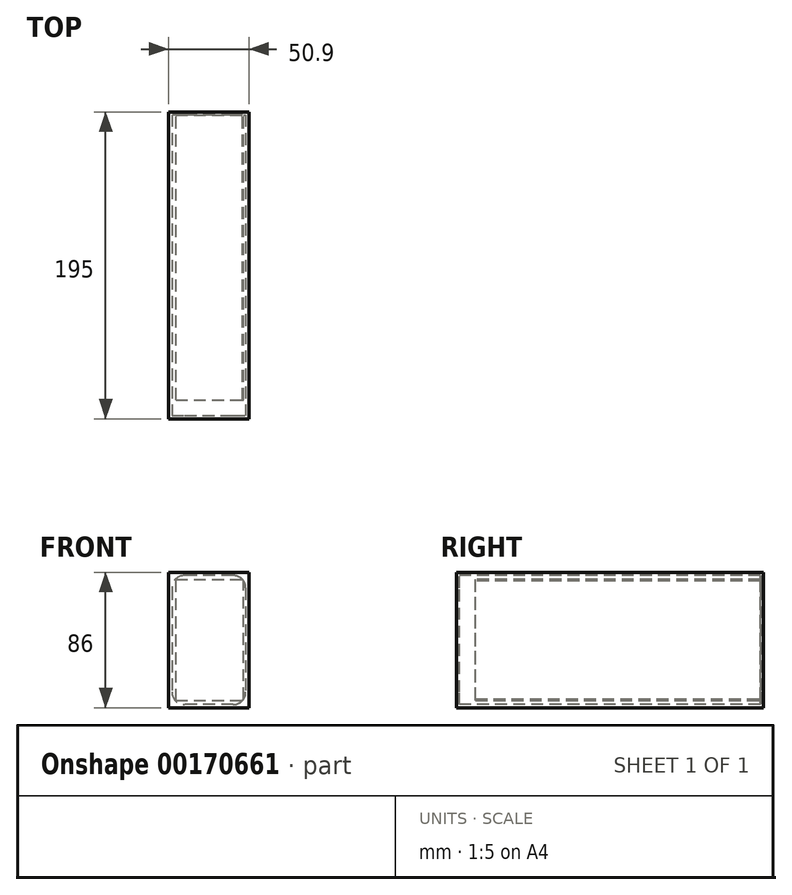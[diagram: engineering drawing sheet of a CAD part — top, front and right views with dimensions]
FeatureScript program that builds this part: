
annotation { "Feature Type Name" : "Feature", "Feature Type Description" : "" }
export const myFeature = defineFeature(function(context is Context, id is Id, definition is map)
    precondition{}
    {
        {
            var Q0;
            Q0=qCreatedBy(makeId("Front.planeOp"),FACE);
            var sketch = newSketch(context, id + "F0", { "sketchPlane" : qUnion([Q0])});
            skLineSegment(sketch, "E0.bottom", {"start": v(-21.5, -38.5) * mm, "end": v(21.5, -38.5) * mm});
            skLineSegment(sketch, "E0.top", {"start": v(-21.5, 38.5) * mm, "end": v(21.5, 38.5) * mm});
            skLineSegment(sketch, "E0.left", {"start": v(-21.5, -38.5) * mm, "end": v(-21.5, 38.5) * mm});
            skLineSegment(sketch, "E0.right", {"start": v(21.5, -38.5) * mm, "end": v(21.5, 38.5) * mm});
            skPoint(sketch, "E0.middle", {"position": v(0, 0) * mm});
            skSolve(sketch);
        }
        {
            var Q0;
            Q0 = qSketchRegion(id + "F0", true);
            extrude(context, id + "F1", {"entities" : qUnion([Q0]), "depth" : 181 * mm});
        }
        {
            var Q0;
            Q0=makeQuery(id+"F1.opExtrude","CAP_FACE",FACE,{"disambiguationData":[OSD([sQuery(id+"F0.wireOp",EDGE,"E0.bottom"),sQuery(id+"F0.wireOp",EDGE,"E0.top"),sQuery(id+"F0.wireOp",EDGE,"E0.left"),sQuery(id+"F0.wireOp",EDGE,"E0.right")])],"isStart":false});
            var sketch = newSketch(context, id + "F2", { "sketchPlane" : qUnion([Q0])});
            skLineSegment(sketch, "E1.0", {"start": v(-26, 43) * mm, "end": v(24.9, 43) * mm});
            skLineSegment(sketch, "E1.1", {"start": v(-26, -43) * mm, "end": v(-26, 43) * mm});
            skLineSegment(sketch, "E1.2", {"start": v(-26, -43) * mm, "end": v(24.9, -43) * mm});
            skLineSegment(sketch, "E1.3", {"start": v(24.9, -43) * mm, "end": v(24.9, 43) * mm});
            skLineSegment(sketch, "E2.0", {"start": v(-24, -41) * mm, "end": v(-24, 41) * mm});
            skLineSegment(sketch, "E2.1", {"start": v(-24, -41) * mm, "end": v(22.9, -41) * mm});
            skLineSegment(sketch, "E2.2", {"start": v(22.9, -41) * mm, "end": v(22.9, 41) * mm});
            skLineSegment(sketch, "E2.3", {"start": v(-24, 41) * mm, "end": v(22.9, 41) * mm});
            skSolve(sketch);
        }
        {
            var Q0;
            Q0 = qSketchRegion(id + "F2", true);
            var Q1;
            Q1=makeQuery(id+"F2.imprint","IMPRINT",FACE,{"disambiguationData":[TD([[makeQuery(id+"F2.imprint","IMPRINT",EDGE,{"derivedFrom":sQuery(id+"F2.wireOp",EDGE,"YhgQeMUx-xfhY-X2K6-cWPI-3lsgByxm59S8.bottom")}),1.0]])]});
            var Q2;
            Q2=makeQuery(id+"F2.imprint","IMPRINT",FACE,{"disambiguationData":[TD([[makeQuery(id+"F2.imprint","IMPRINT",EDGE,{"derivedFrom":sQuery(id+"F2.wireOp",EDGE,"kugLtaKf-y8IZ-fn6P-hyet-yX94nfG0RmtF.bottom")}),-1.0]])]});
            var Q3;
            Q3=makeQuery(id+"F2.imprint","IMPRINT",FACE,{"disambiguationData":[TD([[makeQuery(id+"F2.imprint","IMPRINT",EDGE,{"derivedFrom":sQuery(id+"F2.wireOp",EDGE,"y0IGXvvy-RBEE-aAOK-xeK6-hANvwNHUVcjb.bottom")}),-1.0]])]});
            var Q4;
            Q4=makeQuery(id+"F2.imprint","IMPRINT",FACE,{"disambiguationData":[TD([[makeQuery(id+"F2.imprint","IMPRINT",EDGE,{"derivedFrom":sQuery(id+"F2.wireOp",EDGE,"i7FCZHbC-8YGg-UAfD-K5Za-r8pBSjdxXD02.bottom")}),1.0]])]});
            var Q5;
            Q5=makeQuery(id+"F1.opExtrude","CAP_FACE",FACE,{"disambiguationData":[OSD([sQuery(id+"F0.wireOp",EDGE,"E0.bottom"),sQuery(id+"F0.wireOp",EDGE,"E0.top"),sQuery(id+"F0.wireOp",EDGE,"E0.left"),sQuery(id+"F0.wireOp",EDGE,"E0.right")])],"isStart":true});
            extrude(context, id + "F3", {"entities" : qUnion([Q0, Q1, Q2, Q3, Q4]), "endBound" : BoundingType.UP_TO_SURFACE, "oppositeDirection" : true, "endBoundEntityFace" : qUnion([Q5]), "depth" : 25 * mm, "hasSecondDirection" : true, "secondDirectionOppositeDirection" : false, "secondDirectionDepth" : 10 * mm});
        }
        {
            var Q0;
            Q0=makeQuery(id+"F3.opExtrude","SWEPT_EDGE",EDGE,{"disambiguationData":[OSD([sQuery(id+"F2.wireOp",EDGE,"E2.0"),sQuery(id+"F2.wireOp",EDGE,"E2.3")])]});
            var Q1;
            Q1=makeQuery(id+"F3.opExtrude","SWEPT_EDGE",EDGE,{"disambiguationData":[OSD([sQuery(id+"F2.wireOp",EDGE,"E2.2"),sQuery(id+"F2.wireOp",EDGE,"E2.3")])]});
            var Q2;
            Q2=makeQuery(id+"F3.opExtrude","SWEPT_EDGE",EDGE,{"disambiguationData":[OSD([sQuery(id+"F2.wireOp",EDGE,"E2.1"),sQuery(id+"F2.wireOp",EDGE,"E2.2")])]});
            var Q3;
            Q3=makeQuery(id+"F3.opExtrude","SWEPT_EDGE",EDGE,{"disambiguationData":[OSD([sQuery(id+"F2.wireOp",EDGE,"E2.0"),sQuery(id+"F2.wireOp",EDGE,"E2.1")])]});
            fillet(context, id + "F4", {"entities" : qUnion([Q0, Q1, Q2, Q3]), "radius" : 8 * mm, "tangentPropagation" : true, "allowEdgeOverflow" : false});
        }
        {
            var Q0;
            Q0=makeQuery(id+"F3.opExtrude","CAP_FACE",FACE,{"disambiguationData":[OSD([sQuery(id+"F2.wireOp",EDGE,"E1.0"),sQuery(id+"F2.wireOp",EDGE,"E1.1"),sQuery(id+"F2.wireOp",EDGE,"E1.2"),sQuery(id+"F2.wireOp",EDGE,"E1.3"),sQuery(id+"F2.wireOp",EDGE,"E2.0"),sQuery(id+"F2.wireOp",EDGE,"E2.1"),sQuery(id+"F2.wireOp",EDGE,"E2.2"),sQuery(id+"F2.wireOp",EDGE,"E2.3")])],"isStart":false});
            var sketch = newSketch(context, id + "F5", { "sketchPlane" : qUnion([Q0])});
            skLineSegment(sketch, "E3.0", {"start": v(-24.9, 43) * mm, "end": v(26, 43) * mm});
            skLineSegment(sketch, "E3.1", {"start": v(-24.9, 43) * mm, "end": v(-24.9, -43) * mm});
            skLineSegment(sketch, "E3.2", {"start": v(26, 43) * mm, "end": v(26, -43) * mm});
            skLineSegment(sketch, "E3.3", {"start": v(-24.9, -43) * mm, "end": v(26, -43) * mm});
            skSolve(sketch);
        }
        {
            var Q0;
            Q0 = qSketchRegion(id + "F5", true);
            extrude(context, id + "F6", {"entities" : qUnion([Q0]), "operationType" : NewBodyOperationType.ADD, "depth" : 2 * mm});
        }
        {
            var Q0;
            Q0=makeQuery(id+"F3.opExtrude","CAP_FACE",FACE,{"disambiguationData":[OSD([sQuery(id+"F2.wireOp",EDGE,"E1.0"),sQuery(id+"F2.wireOp",EDGE,"E1.1"),sQuery(id+"F2.wireOp",EDGE,"E1.2"),sQuery(id+"F2.wireOp",EDGE,"E1.3"),sQuery(id+"F2.wireOp",EDGE,"E2.0"),sQuery(id+"F2.wireOp",EDGE,"E2.1"),sQuery(id+"F2.wireOp",EDGE,"E2.2"),sQuery(id+"F2.wireOp",EDGE,"E2.3")])],"isStart":true});
            var sketch = newSketch(context, id + "F7", { "sketchPlane" : qUnion([Q0])});
            skLineSegment(sketch, "E4.0", {"start": v(-26, 43) * mm, "end": v(24.9, 43) * mm});
            skLineSegment(sketch, "E4.1", {"start": v(-26, -43) * mm, "end": v(-26, 43) * mm});
            skLineSegment(sketch, "E4.2", {"start": v(-26, -43) * mm, "end": v(24.9, -43) * mm});
            skLineSegment(sketch, "E4.3", {"start": v(24.9, -43) * mm, "end": v(24.9, 43) * mm});
            skSolve(sketch);
        }
        {
            var Q0;
            Q0 = qSketchRegion(id + "F7", true);
            extrude(context, id + "F8", {"entities" : qUnion([Q0]), "operationType" : NewBodyOperationType.ADD, "depth" : 2 * mm});
        }
    });
